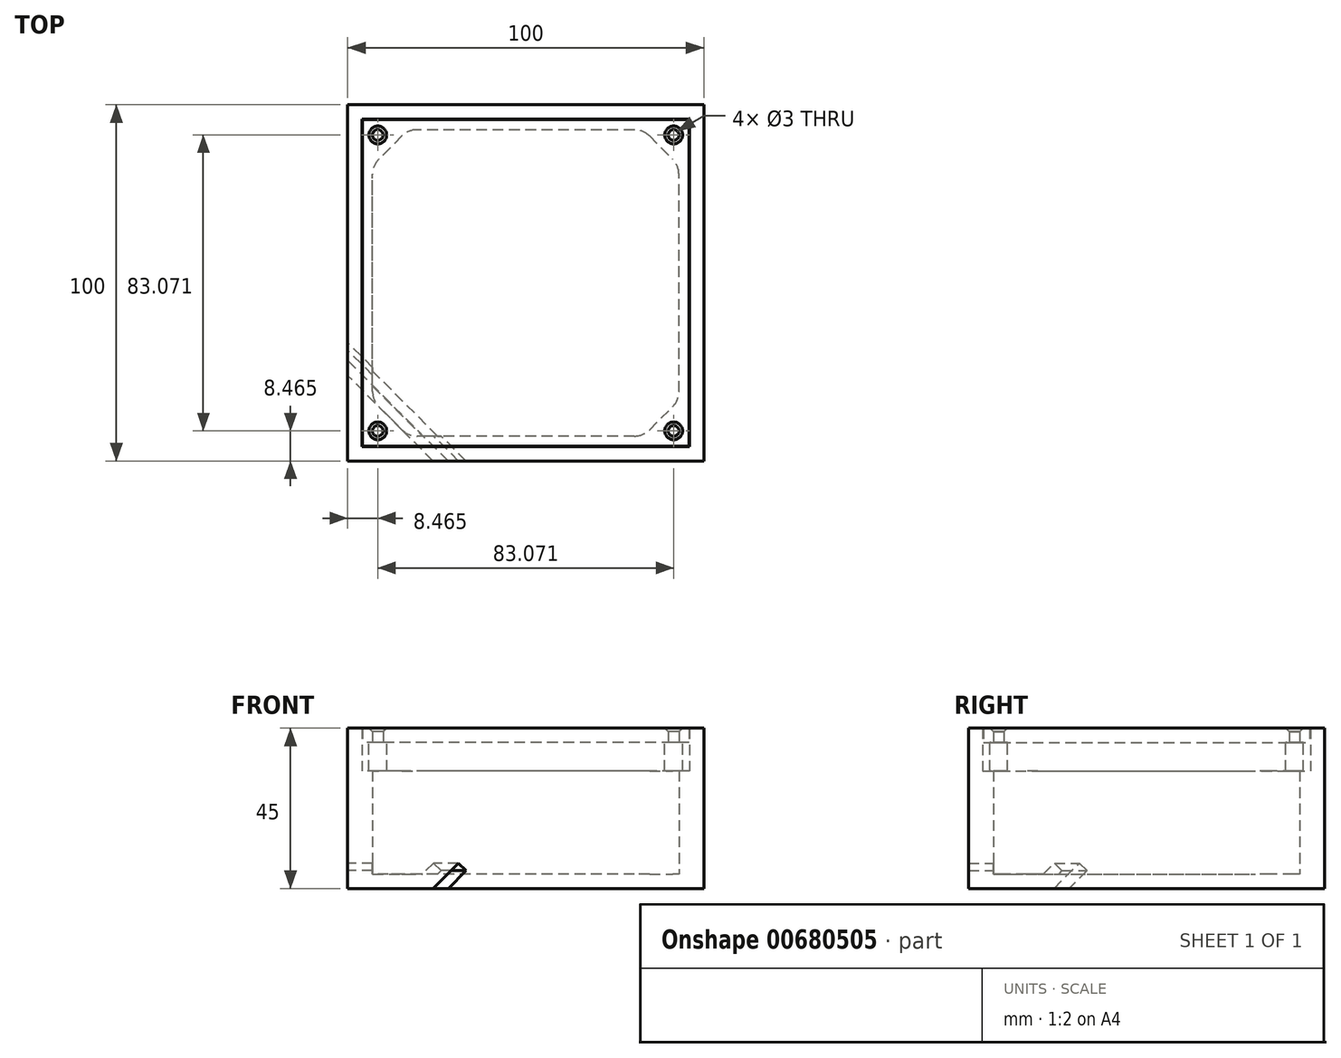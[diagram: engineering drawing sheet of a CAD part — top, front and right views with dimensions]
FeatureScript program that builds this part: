
annotation { "Feature Type Name" : "Feature", "Feature Type Description" : "" }
export const myFeature = defineFeature(function(context is Context, id is Id, definition is map)
    precondition{}
    {
        {
            var Q0;
            Q0=qCreatedBy(makeId("Top.planeOp"),FACE);
            var sketch = newSketch(context, id + "F0", { "sketchPlane" : qUnion([Q0])});
            skLineSegment(sketch, "E0.bottom", {"start": v(50, -50) * mm, "end": v(-50, -50) * mm});
            skLineSegment(sketch, "E0.top", {"start": v(50, 50) * mm, "end": v(-50, 50) * mm});
            skLineSegment(sketch, "E0.left", {"start": v(50, -50) * mm, "end": v(50, 50) * mm});
            skLineSegment(sketch, "E0.right", {"start": v(-50, -50) * mm, "end": v(-50, 50) * mm});
            skPoint(sketch, "E0.middle", {"position": v(0, 0) * mm});
            skLineSegment(sketch, "E1.0", {"start": v(46, 46) * mm, "end": v(-46, 46) * mm});
            skLineSegment(sketch, "E1.1", {"start": v(46, -46) * mm, "end": v(46, 46) * mm});
            skLineSegment(sketch, "E1.2", {"start": v(46, -46) * mm, "end": v(-46, -46) * mm});
            skLineSegment(sketch, "E1.3", {"start": v(-46, -46) * mm, "end": v(-46, 46) * mm});
            skLineSegment(sketch, "E2.0", {"start": v(30.51, 43) * mm, "end": v(-30.51, 43) * mm});
            skLineSegment(sketch, "E2.1", {"start": v(43, -30.51) * mm, "end": v(43, 30.51) * mm});
            skLineSegment(sketch, "E2.2", {"start": v(30.51, -43) * mm, "end": v(-30.51, -43) * mm});
            skLineSegment(sketch, "E2.3", {"start": v(-43, -30.51) * mm, "end": v(-43, 30.51) * mm});
            skLineSegment(sketch, "E3", {"start": v(-34.76, 41.24) * mm, "end": v(-41.24, 34.76) * mm});
            skLineSegment(sketch, "E4", {"start": v(0, 5.97) * mm, "end": v(0, -4.1) * mm, "construction": true});
            skLineSegment(sketch, "E5", {"start": v(-7.17, 0) * mm, "end": v(9.09, 0) * mm, "construction": true});
            skLineSegment(sketch, "E6.MirrorCS", {"start": v(34.76, 41.24) * mm, "end": v(41.24, 34.76) * mm});
            skLineSegment(sketch, "E7.MirrorCS", {"start": v(-34.76, -41.24) * mm, "end": v(-41.24, -34.76) * mm});
            skLineSegment(sketch, "E8.MirrorCS", {"start": v(34.76, -41.24) * mm, "end": v(41.24, -34.76) * mm});
            skPoint(sketch, "E9.newPointA", {"position": v(-33, 43) * mm});
            skArc(sketch, "E9.filletArc", {"start": v(-30.51, 43) * mm, "mid": v(-32.81, 42.54) * mm, "end": v(-34.76, 41.24) * mm});
            skPoint(sketch, "E10.newPointA", {"position": v(-43, 33) * mm});
            skArc(sketch, "E10.filletArc", {"start": v(-41.24, 34.76) * mm, "mid": v(-42.54, 32.81) * mm, "end": v(-43, 30.51) * mm});
            skPoint(sketch, "E11.newPointB", {"position": v(-43, -33) * mm});
            skArc(sketch, "E11.filletArc", {"start": v(-43, -30.51) * mm, "mid": v(-42.54, -32.81) * mm, "end": v(-41.24, -34.76) * mm});
            skPoint(sketch, "E12.newPointA", {"position": v(-33, -43) * mm});
            skArc(sketch, "E12.filletArc", {"start": v(-34.76, -41.24) * mm, "mid": v(-32.81, -42.54) * mm, "end": v(-30.51, -43) * mm});
            skPoint(sketch, "E13.newPointB", {"position": v(33, -43) * mm});
            skArc(sketch, "E13.filletArc", {"start": v(30.51, -43) * mm, "mid": v(32.81, -42.54) * mm, "end": v(34.76, -41.24) * mm});
            skPoint(sketch, "E14.newPointA", {"position": v(43, -33) * mm});
            skArc(sketch, "E14.filletArc", {"start": v(41.24, -34.76) * mm, "mid": v(42.54, -32.81) * mm, "end": v(43, -30.51) * mm});
            skPoint(sketch, "E15.newPointB", {"position": v(43, 33) * mm});
            skArc(sketch, "E15.filletArc", {"start": v(43, 30.51) * mm, "mid": v(42.54, 32.81) * mm, "end": v(41.24, 34.76) * mm});
            skPoint(sketch, "E16.newPointB", {"position": v(33, 43) * mm});
            skArc(sketch, "E16.filletArc", {"start": v(34.76, 41.24) * mm, "mid": v(32.81, 42.54) * mm, "end": v(30.51, 43) * mm});
            skSolve(sketch);
        }
        {
            var Q0;
            Q0=makeQuery(id+"F0.imprint","IMPRINT",FACE,{"disambiguationData":[TD([[makeQuery(id+"F0.imprint","IMPRINT",EDGE,{"derivedFrom":sQuery(id+"F0.wireOp",EDGE,"E0.bottom")}),-1.0]])]});
            extrude(context, id + "F1", {"entities" : qUnion([Q0]), "depth" : 45 * mm, "offsetDistance" : 25 * mm});
        }
        {
            var Q0;
            Q0=makeQuery(id+"F0.imprint","IMPRINT",FACE,{"disambiguationData":[TD([[makeQuery(id+"F0.imprint","IMPRINT",EDGE,{"derivedFrom":sQuery(id+"F0.wireOp",EDGE,"E1.0")}),1.0]])]});
            extrude(context, id + "F2", {"entities" : qUnion([Q0]), "operationType" : NewBodyOperationType.ADD, "depth" : 41 * mm, "offsetDistance" : 25 * mm});
        }
        {
            var Q0;
            Q0=makeQuery(id+"F0.imprint","IMPRINT",FACE,{"disambiguationData":[TD([[makeQuery(id+"F0.imprint","IMPRINT",EDGE,{"derivedFrom":sQuery(id+"F0.wireOp",EDGE,"E1.0")}),1.0]])]});
            var Q1;
            Q1=makeQuery(id+"F0.imprint","IMPRINT",FACE,{"disambiguationData":[TD([[makeQuery(id+"F0.imprint","IMPRINT",EDGE,{"derivedFrom":sQuery(id+"F0.wireOp",EDGE,"E2.0")}),1.0]])]});
            extrude(context, id + "F3", {"entities" : qUnion([Q0, Q1]), "operationType" : NewBodyOperationType.ADD, "depth" : 4 * mm, "offsetDistance" : 25 * mm});
        }
        {
            var Q0;
            Q0=makeQuery(id+"F0.imprint","IMPRINT",FACE,{"disambiguationData":[TD([[makeQuery(id+"F0.imprint","IMPRINT",EDGE,{"derivedFrom":sQuery(id+"F0.wireOp",EDGE,"E0.bottom")}),-1.0]])]});
            var sketch = newSketch(context, id + "F4", { "sketchPlane" : qUnion([Q0])});
            skLineSegment(sketch, "E17.0", {"start": v(50, -50) * mm, "end": v(-50, -50) * mm});
            skLineSegment(sketch, "E18.0", {"start": v(-50, -50) * mm, "end": v(-50, 50) * mm});
            skLineSegment(sketch, "E19.0", {"start": v(50, 50) * mm, "end": v(-50, 50) * mm});
            skLineSegment(sketch, "E20.0", {"start": v(50, -50) * mm, "end": v(50, 50) * mm});
            skLineSegment(sketch, "E21.0.0", {"start": v(-30.51, -43) * mm, "end": v(30.51, -43) * mm});
            skArc(sketch, "E21.0.1", {"start": v(30.51, -43) * mm, "mid": v(32.81, -42.54) * mm, "end": v(34.76, -41.24) * mm});
            skLineSegment(sketch, "E21.0.2", {"start": v(34.76, -41.24) * mm, "end": v(41.24, -34.76) * mm});
            skArc(sketch, "E21.0.3", {"start": v(41.24, -34.76) * mm, "mid": v(42.54, -32.81) * mm, "end": v(43, -30.51) * mm});
            skLineSegment(sketch, "E21.0.4", {"start": v(43, -30.51) * mm, "end": v(43, 30.51) * mm});
            skArc(sketch, "E21.0.5", {"start": v(43, 30.51) * mm, "mid": v(42.54, 32.81) * mm, "end": v(41.24, 34.76) * mm});
            skLineSegment(sketch, "E21.0.6", {"start": v(41.24, 34.76) * mm, "end": v(34.76, 41.24) * mm});
            skArc(sketch, "E21.0.7", {"start": v(34.76, 41.24) * mm, "mid": v(32.81, 42.54) * mm, "end": v(30.51, 43) * mm});
            skLineSegment(sketch, "E21.0.8", {"start": v(30.51, 43) * mm, "end": v(-30.51, 43) * mm});
            skArc(sketch, "E21.0.9", {"start": v(-30.51, 43) * mm, "mid": v(-32.81, 42.54) * mm, "end": v(-34.76, 41.24) * mm});
            skLineSegment(sketch, "E21.0.10", {"start": v(-34.76, 41.24) * mm, "end": v(-41.24, 34.76) * mm});
            skArc(sketch, "E21.0.11", {"start": v(-41.24, 34.76) * mm, "mid": v(-42.54, 32.81) * mm, "end": v(-43, 30.51) * mm});
            skLineSegment(sketch, "E21.0.12", {"start": v(-43, 30.51) * mm, "end": v(-43, -30.51) * mm});
            skArc(sketch, "E21.0.13", {"start": v(-43, -30.51) * mm, "mid": v(-42.54, -32.81) * mm, "end": v(-41.24, -34.76) * mm});
            skLineSegment(sketch, "E21.0.14", {"start": v(-41.24, -34.76) * mm, "end": v(-34.76, -41.24) * mm});
            skArc(sketch, "E21.0.15", {"start": v(-34.76, -41.24) * mm, "mid": v(-32.81, -42.54) * mm, "end": v(-30.51, -43) * mm});
            skLineSegment(sketch, "E22.0.0", {"start": v(-46, 46) * mm, "end": v(-46, -46) * mm});
            skLineSegment(sketch, "E22.0.1", {"start": v(-46, -46) * mm, "end": v(46, -46) * mm});
            skLineSegment(sketch, "E22.0.2", {"start": v(46, -46) * mm, "end": v(46, 46) * mm});
            skLineSegment(sketch, "E22.0.3", {"start": v(46, 46) * mm, "end": v(-46, 46) * mm});
            skLineSegment(sketch, "E23", {"start": v(-14.9, -61.1) * mm, "end": v(-57.84, -18.16) * mm});
            skLineSegment(sketch, "E24", {"start": v(-16.5, -55.25) * mm, "end": v(-59.43, -12.32) * mm, "construction": true});
            skPoint(sketch, "E25", {"position": v(-50, -21.76) * mm});
            skPoint(sketch, "E26", {"position": v(-50, -26) * mm});
            skPoint(sketch, "E27", {"position": v(-26, -50) * mm});
            skPoint(sketch, "E28", {"position": v(-21.76, -50) * mm});
            skSolve(sketch);
        }
        {
            var Q0;
            Q0=makeQuery(id+"F1.opExtrude","SWEPT_FACE",FACE,{"disambiguationData":[OSD([sQuery(id+"F0.wireOp",EDGE,"E0.right")])]});
            var sketch = newSketch(context, id + "F5", { "sketchPlane" : qUnion([Q0])});
            skLineSegment(sketch, "E29", {"start": v(21.76, 0) * mm, "end": v(16.76, 5) * mm});
            skLineSegment(sketch, "E30", {"start": v(26, 0) * mm, "end": v(18.88, 7.12) * mm});
            skLineSegment(sketch, "E31", {"start": v(16.76, 5) * mm, "end": v(18.88, 7.12) * mm});
            skLineSegment(sketch, "E32", {"start": v(21.76, 0) * mm, "end": v(26, 0) * mm});
            skSolve(sketch);
        }
        {
            var Q0;
            Q0=makeQuery(id+"F5.imprint","IMPRINT",FACE,{"disambiguationData":[TD([[makeQuery(id+"F5.imprint","IMPRINT",EDGE,{"derivedFrom":sQuery(id+"F5.wireOp",EDGE,"E29")}),-1.0]])]});
            var Q1;
            Q1=sQuery(id+"F4.wireOp",EDGE,"E23");
            sweep(context, id + "F6", {"operationType" : NewBodyOperationType.REMOVE, "profiles" : qUnion([Q0]), "path" : qUnion([Q1])});
        }
        {
            var Q0;
            Q0=makeQuery(id+"F2.opExtrude","CAP_FACE",FACE,{"disambiguationData":[OSD([sQuery(id+"F0.wireOp",EDGE,"E1.0"),sQuery(id+"F0.wireOp",EDGE,"E1.1"),sQuery(id+"F0.wireOp",EDGE,"E1.2"),sQuery(id+"F0.wireOp",EDGE,"E1.3"),sQuery(id+"F0.wireOp",EDGE,"E2.0"),sQuery(id+"F0.wireOp",EDGE,"E2.1"),sQuery(id+"F0.wireOp",EDGE,"E2.2"),sQuery(id+"F0.wireOp",EDGE,"E2.3"),sQuery(id+"F0.wireOp",EDGE,"E3"),sQuery(id+"F0.wireOp",EDGE,"E6.MirrorCS"),sQuery(id+"F0.wireOp",EDGE,"E7.MirrorCS"),sQuery(id+"F0.wireOp",EDGE,"E8.MirrorCS"),sQuery(id+"F0.wireOp",EDGE,"E9.filletArc"),sQuery(id+"F0.wireOp",EDGE,"E10.filletArc"),sQuery(id+"F0.wireOp",EDGE,"E11.filletArc"),sQuery(id+"F0.wireOp",EDGE,"E12.filletArc"),sQuery(id+"F0.wireOp",EDGE,"E13.filletArc"),sQuery(id+"F0.wireOp",EDGE,"E14.filletArc"),sQuery(id+"F0.wireOp",EDGE,"E15.filletArc"),sQuery(id+"F0.wireOp",EDGE,"E16.filletArc")])],"isStart":false});
            var sketch = newSketch(context, id + "F7", { "sketchPlane" : qUnion([Q0])});
            skCircle(sketch, "E33", {"center": v(-41.54, 41.54) * mm, "radius": 2.5 * mm});
            skCircle(sketch, "E34.MirrorC", {"center": v(41.54, 41.54) * mm, "radius": 2.5 * mm});
            skCircle(sketch, "E35.MirrorC", {"center": v(-41.54, -41.54) * mm, "radius": 2.5 * mm});
            skCircle(sketch, "E36.MirrorC", {"center": v(41.54, -41.54) * mm, "radius": 2.5 * mm});
            skSolve(sketch);
        }
        {
            var Q0;
            Q0=makeQuery(id+"F7.imprint","IMPRINT",FACE,{"disambiguationData":[TD([[makeQuery(id+"F7.imprint","IMPRINT",EDGE,{"derivedFrom":sQuery(id+"F7.wireOp",EDGE,"E33")}),1.0]])]});
            var Q1;
            Q1=makeQuery(id+"F7.imprint","IMPRINT",FACE,{"disambiguationData":[TD([[makeQuery(id+"F7.imprint","IMPRINT",EDGE,{"derivedFrom":sQuery(id+"F7.wireOp",EDGE,"E34.MirrorC")}),-1.0]])]});
            var Q2;
            Q2=makeQuery(id+"F7.imprint","IMPRINT",FACE,{"disambiguationData":[TD([[makeQuery(id+"F7.imprint","IMPRINT",EDGE,{"derivedFrom":sQuery(id+"F7.wireOp",EDGE,"E36.MirrorC")}),1.0]])]});
            var Q3;
            Q3=makeQuery(id+"F7.imprint","IMPRINT",FACE,{"disambiguationData":[TD([[makeQuery(id+"F7.imprint","IMPRINT",EDGE,{"derivedFrom":sQuery(id+"F7.wireOp",EDGE,"E35.MirrorC")}),-1.0]])]});
            extrude(context, id + "F8", {"entities" : qUnion([Q0, Q1, Q2, Q3]), "operationType" : NewBodyOperationType.REMOVE, "oppositeDirection" : true, "depth" : 8 * mm, "offsetDistance" : 25 * mm});
        }
        {
            var Q0;
            Q0=makeQuery(id+"F2.opExtrude","CAP_FACE",FACE,{"disambiguationData":[OSD([sQuery(id+"F0.wireOp",EDGE,"E1.0"),sQuery(id+"F0.wireOp",EDGE,"E1.1"),sQuery(id+"F0.wireOp",EDGE,"E1.2"),sQuery(id+"F0.wireOp",EDGE,"E1.3"),sQuery(id+"F0.wireOp",EDGE,"E2.0"),sQuery(id+"F0.wireOp",EDGE,"E2.1"),sQuery(id+"F0.wireOp",EDGE,"E2.2"),sQuery(id+"F0.wireOp",EDGE,"E2.3"),sQuery(id+"F0.wireOp",EDGE,"E3"),sQuery(id+"F0.wireOp",EDGE,"E6.MirrorCS"),sQuery(id+"F0.wireOp",EDGE,"E7.MirrorCS"),sQuery(id+"F0.wireOp",EDGE,"E8.MirrorCS"),sQuery(id+"F0.wireOp",EDGE,"E9.filletArc"),sQuery(id+"F0.wireOp",EDGE,"E10.filletArc"),sQuery(id+"F0.wireOp",EDGE,"E11.filletArc"),sQuery(id+"F0.wireOp",EDGE,"E12.filletArc"),sQuery(id+"F0.wireOp",EDGE,"E13.filletArc"),sQuery(id+"F0.wireOp",EDGE,"E14.filletArc"),sQuery(id+"F0.wireOp",EDGE,"E15.filletArc"),sQuery(id+"F0.wireOp",EDGE,"E16.filletArc")])],"isStart":false});
            var sketch = newSketch(context, id + "F9", { "sketchPlane" : qUnion([Q0])});
            skLineSegment(sketch, "E37.0", {"start": v(45.8, 45.8) * mm, "end": v(-45.8, 45.8) * mm});
            skLineSegment(sketch, "E37.1", {"start": v(45.8, -45.8) * mm, "end": v(45.8, 45.8) * mm});
            skLineSegment(sketch, "E37.2", {"start": v(45.8, -45.8) * mm, "end": v(-45.8, -45.8) * mm});
            skLineSegment(sketch, "E37.3", {"start": v(-45.8, -45.8) * mm, "end": v(-45.8, 45.8) * mm});
            skCircle(sketch, "E38.0", {"center": v(-41.54, 41.54) * mm, "radius": 1.5 * mm});
            skCircle(sketch, "E39.0", {"center": v(-41.54, -41.54) * mm, "radius": 1.5 * mm});
            skCircle(sketch, "E40.0", {"center": v(41.54, 41.54) * mm, "radius": 1.5 * mm});
            skCircle(sketch, "E41.0", {"center": v(41.54, -41.54) * mm, "radius": 1.5 * mm});
            skSolve(sketch);
        }
        {
            var Q0;
            Q0=makeQuery(id+"F9.imprint","IMPRINT",FACE,{"disambiguationData":[TD([[makeQuery(id+"F9.imprint","IMPRINT",EDGE,{"derivedFrom":makeQuery(id+"F2.opExtrude","CAP_EDGE",EDGE,{"disambiguationData":[OSD([sQuery(id+"F0.wireOp",EDGE,"E2.0")])],"isStart":false})}),1.0]])]});
            var Q1;
            Q1=makeQuery(id+"F9.imprint","IMPRINT",FACE,{"disambiguationData":[TD([[makeQuery(id+"F9.imprint","IMPRINT",EDGE,{"derivedFrom":sQuery(id+"F9.wireOp",EDGE,"E37.0")}),1.0]])]});
            var Q2;
            Q2=makeQuery(id+"F9.imprint","IMPRINT",FACE,{"disambiguationData":[TD([[makeQuery(id+"F9.imprint","IMPRINT",EDGE,{"derivedFrom":sQuery(id+"F9.wireOp",EDGE,"E38.0")}),-1.0]])]});
            var Q3;
            Q3=makeQuery(id+"F9.imprint","IMPRINT",FACE,{"disambiguationData":[TD([[makeQuery(id+"F9.imprint","IMPRINT",EDGE,{"derivedFrom":sQuery(id+"F9.wireOp",EDGE,"E39.0")}),-1.0]])]});
            var Q4;
            Q4=makeQuery(id+"F9.imprint","IMPRINT",FACE,{"disambiguationData":[TD([[makeQuery(id+"F9.imprint","IMPRINT",EDGE,{"derivedFrom":sQuery(id+"F9.wireOp",EDGE,"E41.0")}),-1.0]])]});
            var Q5;
            Q5=makeQuery(id+"F9.imprint","IMPRINT",FACE,{"disambiguationData":[TD([[makeQuery(id+"F9.imprint","IMPRINT",EDGE,{"derivedFrom":sQuery(id+"F9.wireOp",EDGE,"E40.0")}),-1.0]])]});
            extrude(context, id + "F10", {"entities" : qUnion([Q0, Q1, Q2, Q3, Q4, Q5]), "depth" : 4 * mm, "offsetDistance" : 25 * mm});
        }
        {
            var Q0;
            Q0=makeQuery(id+"F10.opExtrude","CAP_EDGE",EDGE,{"disambiguationData":[OSD([sQuery(id+"F9.wireOp",EDGE,"E38.0")])],"isStart":false});
            var Q1;
            Q1=makeQuery(id+"F10.opExtrude","CAP_EDGE",EDGE,{"disambiguationData":[OSD([sQuery(id+"F9.wireOp",EDGE,"E40.0")])],"isStart":false});
            var Q2;
            Q2=makeQuery(id+"F10.opExtrude","CAP_EDGE",EDGE,{"disambiguationData":[OSD([sQuery(id+"F9.wireOp",EDGE,"E39.0")])],"isStart":false});
            var Q3;
            Q3=makeQuery(id+"F10.opExtrude","CAP_EDGE",EDGE,{"disambiguationData":[OSD([sQuery(id+"F9.wireOp",EDGE,"E41.0")])],"isStart":false});
            chamfer(context, id + "F11", {"entities" : qUnion([Q0, Q1, Q2, Q3]), "width" : 1 * mm, "tangentPropagation" : true});
        }
    });
